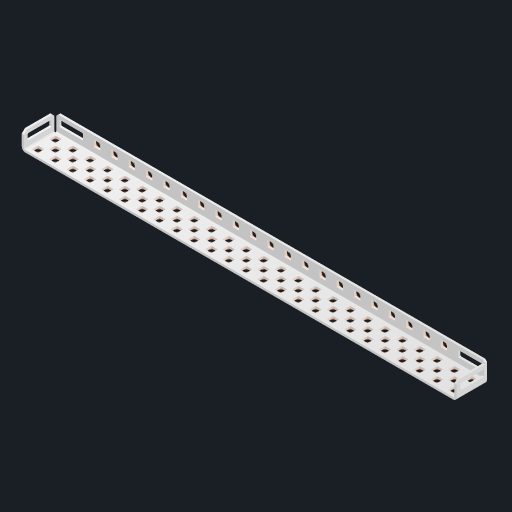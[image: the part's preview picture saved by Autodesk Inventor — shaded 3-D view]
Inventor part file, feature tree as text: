
AUTODESK INVENTOR PART (.ipt)
format: ipt  version: 2023 (Build 270158030, 158C)  size: 1,610,240 bytes
history: native  units: in
note: dims shown in document units (in); Inventor stores cm internally (conversion verified against a paired STEP export)
features: other x96, extrude x95, pattern_linear x3, sketch x3, chamfer x1, move_body x1, imported_body x1
ambient origin geometry x8: Origin, YZ Plane, XZ Plane, XY Plane, X Axis, Y Axis, Z Axis, Center Point
bodies: Body1 (feature_tree), Body2 (feature_tree), Body3 (feature_tree), Body4 (feature_tree), Body5 (feature_tree), Body6 (feature_tree), Body7 (feature_tree), Body8 (feature_tree), Body9 (feature_tree), Body10 (feature_tree), Body11 (feature_tree), Body12 (feature_tree), Body13 (feature_tree), Body14 (feature_tree), Body15 (feature_tree), Body16 (feature_tree), Body17 (feature_tree), Body18 (feature_tree), Body19 (feature_tree), Body20 (feature_tree), Body21 (feature_tree), Body22 (feature_tree), Body23 (feature_tree), Body24 (feature_tree), Body25 (feature_tree), Body26 (feature_tree), Body27 (feature_tree), Body28 (feature_tree), Body29 (feature_tree), Body30 (feature_tree), Body31 (feature_tree), Body32 (feature_tree), Body33 (feature_tree), Body34 (feature_tree), Body35 (feature_tree), Body36 (feature_tree), Body37 (feature_tree), Body38 (feature_tree), Body39 (feature_tree), Body40 (feature_tree), Body41 (feature_tree), Body42 (feature_tree), Body43 (feature_tree), Body44 (feature_tree), Body45 (feature_tree), Body46 (feature_tree), Body47 (feature_tree), Body48 (feature_tree), Body49 (feature_tree), Body50 (feature_tree), Body51 (feature_tree), Body52 (feature_tree), Body53 (feature_tree), Body54 (feature_tree), Body55 (feature_tree), Body56 (feature_tree), Body57 (feature_tree), Body58 (feature_tree), Body59 (feature_tree), Body60 (feature_tree), Body61 (feature_tree), Body62 (feature_tree), Body63 (feature_tree), Body64 (feature_tree), Body65 (feature_tree), Body66 (feature_tree), Body67 (feature_tree), Body68 (feature_tree), Body69 (feature_tree), Body70 (feature_tree), Body71 (feature_tree), Body72 (feature_tree), Body73 (feature_tree), Body74 (feature_tree), Body75 (feature_tree), Body76 (feature_tree), Body77 (feature_tree), Body78 (feature_tree), Body79 (feature_tree), Body80 (feature_tree), Body81 (feature_tree), Body82 (feature_tree), Body83 (feature_tree), Body84 (feature_tree), Body85 (feature_tree), Body86 (feature_tree), Body87 (feature_tree), Body88 (feature_tree), Body89 (feature_tree), Body90 (feature_tree), Body91 (feature_tree), Body92 (feature_tree), Body93 (feature_tree), Body94 (feature_tree), Body95 (feature_tree), Body96 (feature_tree)
feature tree (200):
  chamfer  "Chamfer2"  Distance=0.063in
  other  "VL-RAIL-HH21-25 RevA1"
  move_body  "Move Body1"
  pattern_linear  "Rectangular Pattern1"  Count1=25 Spacing1=0.5in
  pattern_linear  "Rectangular Pattern2"  Spacing1=0.063in  [1 undecoded]
  pattern_linear  "Rectangular Pattern3"  Count1=24 Spacing1=0.5in
  imported_body  "Base1"
  sketch  "Sketch1"  dims[d0=180.0deg d1=-3.9725in d2=-0.1955in d3=2.3792in]
  other  "Srf1"
  other  "Srf2"
  other  "Srf3"
  other  "Srf4"
  other  "Srf5"
  other  "Srf6"
  other  "Srf7"
  other  "Srf8"
  other  "Srf9"
  other  "Srf10"
  other  "Srf11"
  other  "Srf12"
  other  "Srf13"
  other  "Srf14"
  other  "Srf15"
  other  "Srf16"
  other  "Srf17"
  other  "Srf18"
  other  "Srf19"
  other  "Srf20"
  other  "Srf21"
  other  "Srf22"
  other  "Srf23"
  other  "Srf24"
  other  "Srf25"
  other  "Srf26"
  other  "Srf27"
  other  "Srf28"
  other  "Srf29"
  other  "Srf30"
  other  "Srf31"
  other  "Srf32"
  other  "Srf33"
  other  "Srf34"
  other  "Srf35"
  other  "Srf36"
  other  "Srf37"
  other  "Srf38"
  other  "Srf39"
  other  "Srf40"
  other  "Srf41"
  other  "Srf42"
  other  "Srf43"
  other  "Srf44"
  other  "Srf45"
  other  "Srf46"
  other  "Srf47"
  other  "Srf48"
  other  "Srf49"
  other  "Srf50"
  sketch  "Sketch2"  dims[d4=0.182in d5=0.063in d6=0.0in d7=9.8425in d9=0.5in d10=0.7874in d12=0.5in]
  other  "Srf51"
  other  "Srf52"
  other  "Srf53"
  other  "Srf54"
  other  "Srf55"
  other  "Srf56"
  other  "Srf57"
  other  "Srf58"
  other  "Srf59"
  other  "Srf60"
  other  "Srf61"
  other  "Srf62"
  other  "Srf63"
  other  "Srf64"
  other  "Srf65"
  other  "Srf66"
  other  "Srf67"
  other  "Srf68"
  other  "Srf69"
  other  "Srf70"
  other  "Srf71"
  other  "Srf72"
  other  "Srf73"
  other  "Srf74"
  sketch  "Sketch3"  dims[d13=0.182in d14=0.063in d15=0.0in d16=9.4488in d18=0.5in d19=0.182in d20=0.063in d21=0.0in d22=8.2677in d24=0.5in d25=0.0in d26=0.0in d27=0.0in d28=0.0in d29=0.0in d30=0.0in d31=0.0in d32=0.0in d33=0.0in d34=0.0in d35=0.0in d36=0.0in d37=0.0in d38=0.0in d39=0.0in d40=0.0in d41=0.0in d42=0.0in d43=0.0in d44=0.0in d45=0.0in d46=0.0in d47=0.0in d48=0.0in d49=0.0in d50=0.0in d51=0.0in d52=0.0in d53=0.0in d54=0.0in d55=0.0in d56=0.0in d57=0.0in d58=0.0in d59=0.0in d60=0.0in d61=0.0in d62=0.0in d63=0.0in d64=0.0in d65=0.0in d66=0.0in d67=0.0in d68=0.0in d69=0.0in d70=0.0in d71=0.0in d72=0.0in d73=0.0in d74=0.0in d75=0.0in d76=0.0in d77=0.0in d78=0.0in d79=0.0in d80=0.0in d81=0.0in d82=0.0in d83=0.0in d84=0.0in d85=0.0in d86=0.0in d87=0.0in d88=0.0in d89=0.0in d90=0.0in d91=0.0in d92=0.0in d93=0.0in d94=0.0in d95=0.0in d96=0.0in d97=0.0in d98=0.0in d99=0.0in d100=0.0in d101=0.0in d102=0.0in d103=0.0in d104=0.0in d105=0.0in d106=0.0in d107=0.0in d108=0.0in d109=0.0in d110=0.0in d111=0.0in d112=0.0in d113=0.0in d114=0.0in d115=0.0in d116=0.0in d117=0.0in d118=0.0in d119=0.0in d120=0.0in d121=0.0in d122=0.0in d123=0.0in d124=0.0in d125=0.0in d126=0.0in d127=0.0in d128=0.0in d129=0.0in d130=0.0in d131=0.0in d132=0.0in d133=0.0in d134=0.0in d135=0.0in d136=0.0in d137=0.0in d138=0.0in d139=0.0in d140=0.0in d141=0.0in d142=0.0in d143=0.0in d144=0.0in d145=0.0in d146=0.0in d147=0.0in d148=0.0in d149=0.0in d150=0.0in d151=0.0in d152=0.0in d153=0.0in d154=0.0in d155=0.0in d156=0.0in d157=0.0in d158=0.0in d159=0.0in d160=0.0in d161=0.0in d162=0.0in d163=0.0in d164=0.0in d165=0.0in d166=0.0in d167=0.0in d168=0.0in d169=0.0in d170=0.0in d171=0.0in d172=0.0in d173=0.0in d174=0.0in d175=0.0in d176=0.0in d177=0.0in d178=0.0in d179=0.0in d180=0.0in d181=0.0in d182=0.0in d183=0.0in d184=0.0in d185=0.0in d186=0.0in d187=0.0in d188=0.0in d189=0.0in d190=0.0in d191=0.0in d192=0.0in d193=0.0in d194=0.0in d195=0.0in d196=0.0in d197=0.0in d198=0.0in d199=0.0in d200=0.0in d201=0.0in d202=0.0in d203=0.0in d204=0.0in d205=0.0in d206=0.0in d207=0.0in d208=0.0in d209=0.0in d210=0.0in d211=0.0in d212=0.0in d213=0.0in d214=0.0in]
  other  "Srf75"
  other  "Srf76"
  other  "Srf77"
  other  "Srf78"
  other  "Srf79"
  other  "Srf80"
  other  "Srf81"
  other  "Srf82"
  other  "Srf83"
  other  "Srf84"
  other  "Srf85"
  other  "Srf86"
  other  "Srf87"
  other  "Srf88"
  other  "Srf89"
  other  "Srf90"
  other  "Srf91"
  other  "Srf92"
  other  "Srf93"
  other  "Srf94"
  other  "Srf95"
  extrude  "ExtrusionSrf1"  Depth=0.182in
  extrude  "ExtrusionSrf51"  Depth=0.063in TaperAngle=0.0deg
  extrude  "ExtrusionSrf75"  Depth=0.5in
  extrude  "ExtrusionSrf2"  TaperAngle=0.0deg  [1 undecoded]
  extrude  "ExtrusionSrf3"  TaperAngle=0.0deg  [1 undecoded]
  extrude  "ExtrusionSrf4"  TaperAngle=0.0deg  [1 undecoded]
  extrude  "ExtrusionSrf5"  TaperAngle=0.0deg  [1 undecoded]
  extrude  "ExtrusionSrf6"  TaperAngle=0.0deg  [1 undecoded]
  extrude  "ExtrusionSrf7"  TaperAngle=0.0deg  [1 undecoded]
  extrude  "ExtrusionSrf8"  TaperAngle=0.0deg  [1 undecoded]
  extrude  "ExtrusionSrf9"  TaperAngle=0.0deg  [1 undecoded]
  extrude  "ExtrusionSrf10"  TaperAngle=0.0deg  [1 undecoded]
  extrude  "ExtrusionSrf11"  TaperAngle=0.0deg  [1 undecoded]
  extrude  "ExtrusionSrf12"  TaperAngle=0.0deg  [1 undecoded]
  extrude  "ExtrusionSrf13"  TaperAngle=0.0deg  [1 undecoded]
  extrude  "ExtrusionSrf14"  TaperAngle=0.0deg  [1 undecoded]
  extrude  "ExtrusionSrf15"  TaperAngle=0.0deg  [1 undecoded]
  extrude  "ExtrusionSrf16"  TaperAngle=0.0deg  [1 undecoded]
  extrude  "ExtrusionSrf17"  TaperAngle=0.0deg  [1 undecoded]
  extrude  "ExtrusionSrf18"  TaperAngle=0.0deg  [1 undecoded]
  extrude  "ExtrusionSrf19"  TaperAngle=0.0deg  [1 undecoded]
  extrude  "ExtrusionSrf20"  TaperAngle=0.0deg  [1 undecoded]
  extrude  "ExtrusionSrf21"  TaperAngle=0.0deg  [1 undecoded]
  extrude  "ExtrusionSrf22"  TaperAngle=0.0deg  [1 undecoded]
  extrude  "ExtrusionSrf23"  TaperAngle=0.0deg  [1 undecoded]
  extrude  "ExtrusionSrf24"  TaperAngle=0.0deg  [1 undecoded]
  extrude  "ExtrusionSrf25"  TaperAngle=0.0deg  [1 undecoded]
  extrude  "ExtrusionSrf26"  TaperAngle=0.0deg  [1 undecoded]
  extrude  "ExtrusionSrf27"  TaperAngle=0.0deg  [1 undecoded]
  extrude  "ExtrusionSrf28"  TaperAngle=0.0deg  [1 undecoded]
  extrude  "ExtrusionSrf29"  TaperAngle=0.0deg  [1 undecoded]
  extrude  "ExtrusionSrf30"  TaperAngle=0.0deg  [1 undecoded]
  extrude  "ExtrusionSrf31"  TaperAngle=0.0deg  [1 undecoded]
  extrude  "ExtrusionSrf32"  TaperAngle=0.0deg  [1 undecoded]
  extrude  "ExtrusionSrf33"  TaperAngle=0.0deg  [1 undecoded]
  extrude  "ExtrusionSrf34"  TaperAngle=0.0deg  [1 undecoded]
  extrude  "ExtrusionSrf35"  TaperAngle=0.0deg  [1 undecoded]
  extrude  "ExtrusionSrf36"  TaperAngle=0.0deg  [1 undecoded]
  extrude  "ExtrusionSrf37"  TaperAngle=0.0deg  [1 undecoded]
  extrude  "ExtrusionSrf38"  TaperAngle=0.0deg  [1 undecoded]
  extrude  "ExtrusionSrf39"  TaperAngle=0.0deg  [1 undecoded]
  extrude  "ExtrusionSrf40"  TaperAngle=0.0deg  [1 undecoded]
  extrude  "ExtrusionSrf41"  TaperAngle=0.0deg  [1 undecoded]
  extrude  "ExtrusionSrf42"  TaperAngle=0.0deg  [1 undecoded]
  extrude  "ExtrusionSrf43"  TaperAngle=0.0deg  [1 undecoded]
  extrude  "ExtrusionSrf44"  TaperAngle=0.0deg  [1 undecoded]
  extrude  "ExtrusionSrf45"  TaperAngle=0.0deg  [1 undecoded]
  extrude  "ExtrusionSrf46"  TaperAngle=0.0deg  [1 undecoded]
  extrude  "ExtrusionSrf47"  TaperAngle=0.0deg  [1 undecoded]
  extrude  "ExtrusionSrf48"  TaperAngle=0.0deg  [1 undecoded]
  extrude  "ExtrusionSrf49"  TaperAngle=0.0deg  [1 undecoded]
  extrude  "ExtrusionSrf50"  TaperAngle=0.0deg  [1 undecoded]
  extrude  "ExtrusionSrf52"  TaperAngle=0.0deg  [1 undecoded]
  extrude  "ExtrusionSrf53"  TaperAngle=0.0deg  [1 undecoded]
  extrude  "ExtrusionSrf54"  TaperAngle=0.0deg  [1 undecoded]
  extrude  "ExtrusionSrf55"  TaperAngle=0.0deg  [1 undecoded]
  extrude  "ExtrusionSrf56"  TaperAngle=0.0deg  [1 undecoded]
  extrude  "ExtrusionSrf57"  TaperAngle=0.0deg  [1 undecoded]
  extrude  "ExtrusionSrf58"  TaperAngle=0.0deg  [1 undecoded]
  extrude  "ExtrusionSrf59"  TaperAngle=0.0deg  [1 undecoded]
  extrude  "ExtrusionSrf60"  TaperAngle=0.0deg  [1 undecoded]
  extrude  "ExtrusionSrf61"  TaperAngle=0.0deg  [1 undecoded]
  extrude  "ExtrusionSrf62"  TaperAngle=0.0deg  [1 undecoded]
  extrude  "ExtrusionSrf63"  TaperAngle=0.0deg  [1 undecoded]
  extrude  "ExtrusionSrf64"  TaperAngle=0.0deg  [1 undecoded]
  extrude  "ExtrusionSrf65"  TaperAngle=0.0deg  [1 undecoded]
  extrude  "ExtrusionSrf66"  TaperAngle=0.0deg  [1 undecoded]
  extrude  "ExtrusionSrf67"  TaperAngle=0.0deg  [1 undecoded]
  extrude  "ExtrusionSrf68"  TaperAngle=0.0deg  [1 undecoded]
  extrude  "ExtrusionSrf69"  TaperAngle=0.0deg  [1 undecoded]
  extrude  "ExtrusionSrf70"  TaperAngle=0.0deg  [1 undecoded]
  extrude  "ExtrusionSrf71"  TaperAngle=0.0deg  [1 undecoded]
  extrude  "ExtrusionSrf72"  TaperAngle=0.0deg  [1 undecoded]
  extrude  "ExtrusionSrf73"  TaperAngle=0.0deg  [1 undecoded]
  extrude  "ExtrusionSrf74"  TaperAngle=0.0deg  [1 undecoded]
  extrude  "ExtrusionSrf76"  TaperAngle=0.0deg  [1 undecoded]
  extrude  "ExtrusionSrf77"  TaperAngle=0.0deg  [1 undecoded]
  extrude  "ExtrusionSrf78"  TaperAngle=0.0deg  [1 undecoded]
  extrude  "ExtrusionSrf79"  TaperAngle=0.0deg  [1 undecoded]
  extrude  "ExtrusionSrf80"  TaperAngle=0.0deg  [1 undecoded]
  extrude  "ExtrusionSrf81"  TaperAngle=0.0deg  [1 undecoded]
  extrude  "ExtrusionSrf82"  TaperAngle=0.0deg  [1 undecoded]
  extrude  "ExtrusionSrf83"  TaperAngle=0.0deg  [1 undecoded]
  extrude  "ExtrusionSrf84"  TaperAngle=0.0deg  [1 undecoded]
  extrude  "ExtrusionSrf85"  TaperAngle=0.0deg  [1 undecoded]
  extrude  "ExtrusionSrf86"  TaperAngle=0.0deg  [1 undecoded]
  extrude  "ExtrusionSrf87"  TaperAngle=0.0deg  [1 undecoded]
  extrude  "ExtrusionSrf88"  TaperAngle=0.0deg  [1 undecoded]
  extrude  "ExtrusionSrf89"  TaperAngle=0.0deg  [1 undecoded]
  extrude  "ExtrusionSrf90"  TaperAngle=0.0deg  [1 undecoded]
  extrude  "ExtrusionSrf91"  TaperAngle=0.0deg  [1 undecoded]
  extrude  "ExtrusionSrf92"  TaperAngle=0.0deg  [1 undecoded]
  extrude  "ExtrusionSrf93"  TaperAngle=0.0deg  [1 undecoded]
  extrude  "ExtrusionSrf94"  TaperAngle=0.0deg  [1 undecoded]
  extrude  "ExtrusionSrf95"  TaperAngle=0.0deg  [1 undecoded]
note: 93 required parameter values undecoded (feature->parameter linkage not recoverable at this tier; creation-order binding heuristic only, values carry confidence <= 0.55)
